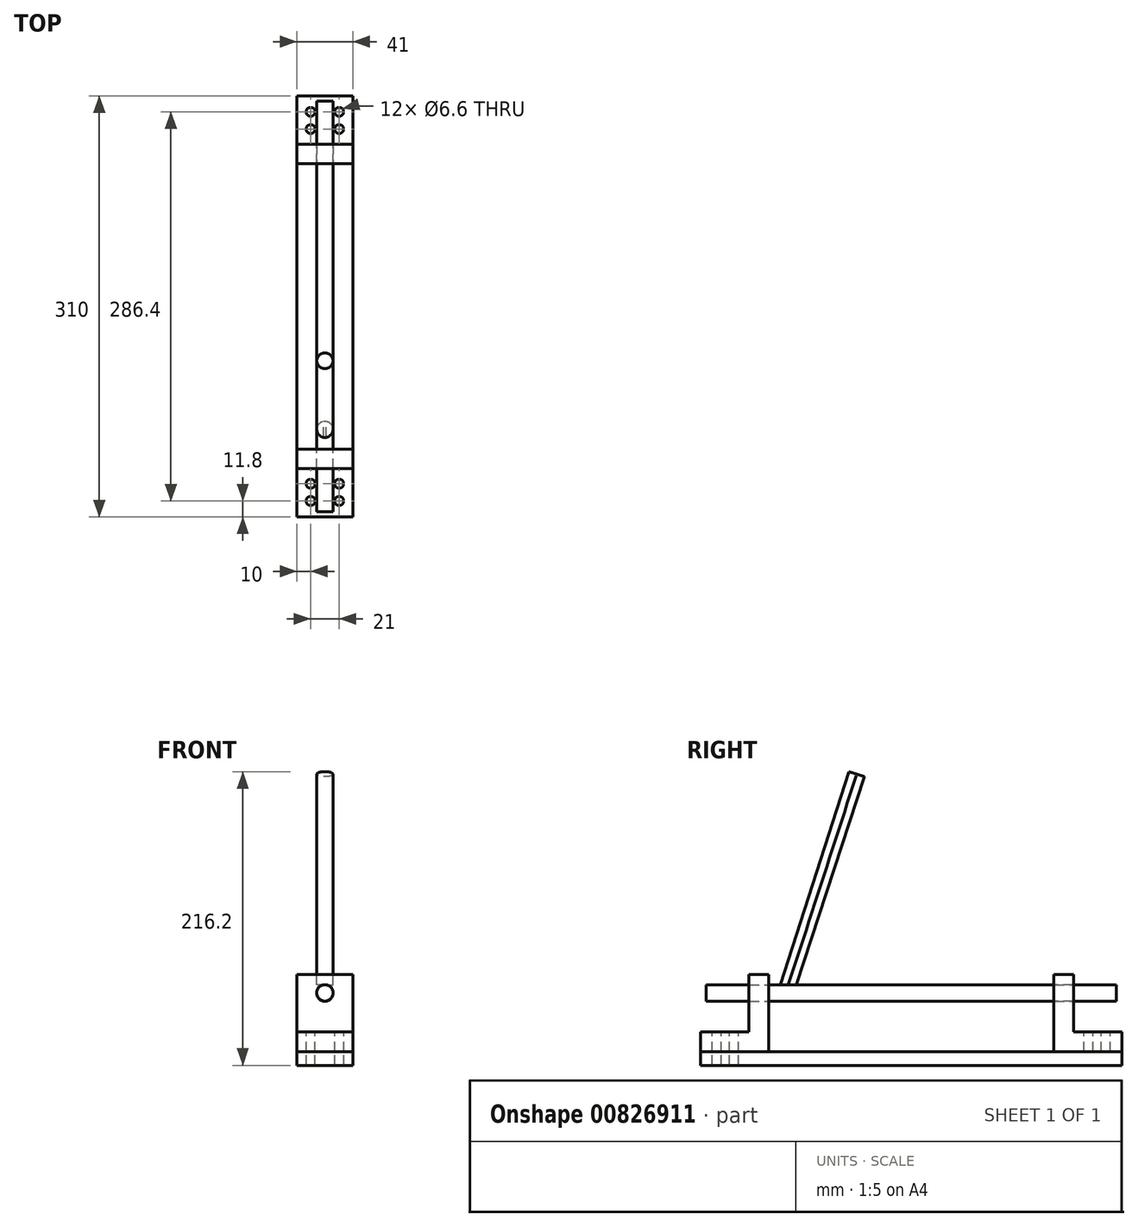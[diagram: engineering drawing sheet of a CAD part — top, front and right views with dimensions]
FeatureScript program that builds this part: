
annotation { "Feature Type Name" : "Feature", "Feature Type Description" : "" }
export const myFeature = defineFeature(function(context is Context, id is Id, definition is map)
    precondition{}
    {
        {
            var Q0;
            Q0=qCreatedBy(makeId("Right.planeOp"),FACE);
            var sketch = newSketch(context, id + "F0", { "sketchPlane" : qUnion([Q0])});
            skLineSegment(sketch, "E0.bottom", {"start": v(-155, -5) * mm, "end": v(155, -5) * mm});
            skLineSegment(sketch, "E0.top", {"start": v(-155, 5) * mm, "end": v(155, 5) * mm});
            skLineSegment(sketch, "E0.left", {"start": v(-155, -5) * mm, "end": v(-155, 5) * mm});
            skLineSegment(sketch, "E0.right", {"start": v(155, -5) * mm, "end": v(155, 5) * mm});
            skSolve(sketch);
        }
        {
            var Q0;
            Q0 = qSketchRegion(id + "F0", true);
            extrude(context, id + "F1", {"entities" : qUnion([Q0]), "depth" : 20.5 * mm, "offsetDistance" : 25.4 * mm, "hasSecondDirection" : true, "secondDirectionOppositeDirection" : true, "secondDirectionDepth" : 20.5 * mm});
        }
        {
            var Q0;
            Q0=qCreatedBy(makeId("Right.planeOp"),FACE);
            var sketch = newSketch(context, id + "F2", { "sketchPlane" : qUnion([Q0])});
            skLineSegment(sketch, "E1.bottom", {"start": v(-155, 5) * mm, "end": v(-105, 5) * mm});
            skLineSegment(sketch, "E1.top", {"start": v(-119.5, 62) * mm, "end": v(-105, 62) * mm});
            skLineSegment(sketch, "E1.left", {"start": v(-155, 5) * mm, "end": v(-155, 19.5) * mm});
            skLineSegment(sketch, "E1.right", {"start": v(-105, 5) * mm, "end": v(-105, 62) * mm});
            skLineSegment(sketch, "E2", {"start": v(-119.5, 62) * mm, "end": v(-119.5, 19.5) * mm});
            skLineSegment(sketch, "E3", {"start": v(-119.5, 19.5) * mm, "end": v(-155, 19.5) * mm});
            skSolve(sketch);
        }
        {
            var Q0;
            Q0=makeQuery(id+"F2.imprint","IMPRINT",FACE,{"disambiguationData":[TD([[makeQuery(id+"F2.imprint","IMPRINT",EDGE,{"derivedFrom":sQuery(id+"F2.wireOp",EDGE,"E1.bottom")}),1.0]])]});
            extrude(context, id + "F3", {"entities" : qUnion([Q0]), "depth" : 20.5 * mm, "offsetDistance" : 25 * mm, "hasSecondDirection" : true, "secondDirectionOppositeDirection" : true, "secondDirectionDepth" : 20.5 * mm});
        }
        {
            var Q0;
            Q0=makeQuery(id+"F3.opExtrude","SWEPT_FACE",FACE,{"disambiguationData":[OSD([sQuery(id+"F2.wireOp",EDGE,"E3")])]});
            var sketch = newSketch(context, id + "F4", { "sketchPlane" : qUnion([Q0])});
            skPoint(sketch, "E4", {"position": v(-10.5, -130.5) * mm});
            skPoint(sketch, "E5", {"position": v(10.5, -130.5) * mm});
            skPoint(sketch, "E6", {"position": v(-10.5, -143.2) * mm});
            skPoint(sketch, "E7", {"position": v(10.5, -143.2) * mm});
            skSolve(sketch);
        }
        {
            var Q0;
            Q0=sQuery(id+"F4.wireOp",VERTEX,"E7");
            var Q1;
            Q1=sQuery(id+"F4.wireOp",VERTEX,"E6");
            var Q2;
            Q2=sQuery(id+"F4.wireOp",VERTEX,"E4");
            var Q3;
            Q3=sQuery(id+"F4.wireOp",VERTEX,"E5");
            var Q4;
            Q4=makeQuery(id+"F1.opExtrude","SWEPT_BODY",BODY,{"disambiguationData":[OSD([sQuery(id+"F0.wireOp",EDGE,"E0.bottom"),sQuery(id+"F0.wireOp",EDGE,"E0.top"),sQuery(id+"F0.wireOp",EDGE,"E0.left"),sQuery(id+"F0.wireOp",EDGE,"E0.right")])]});
            var Q5;
            Q5=makeQuery(id+"F3.opExtrude","SWEPT_BODY",BODY,{"disambiguationData":[OSD([sQuery(id+"F2.wireOp",EDGE,"E1.bottom"),sQuery(id+"F2.wireOp",EDGE,"E1.top"),sQuery(id+"F2.wireOp",EDGE,"E1.left"),sQuery(id+"F2.wireOp",EDGE,"E1.right"),sQuery(id+"F2.wireOp",EDGE,"E2"),sQuery(id+"F2.wireOp",EDGE,"E3")])]});
            hole(context, id + "F5", {"style" : HoleStyle.SIMPLE, "endStyle" : HoleEndStyle.THROUGH, "standardTappedOrClearance" : lookupTablePath({ "standard" : "ISO", "fit" : "Normal", "size" : "M6", "type" : "Clearance" }), "standardBlindInLast" : lookupTablePath({ "fit" : "Standard", "standard" : "ISO", "size" : "M6", "type" : "Clearance" }), "holeDiameter" : 6.6 * mm, "majorDiameter" : 5 * mm, "isTappedThrough" : true, "tappedDepth" : 12 * mm, "tapClearance" : 3, "locations" : qUnion([Q0, Q1, Q2, Q3]), "scope" : qUnion([Q4, Q5])});
        }
        {
            var Q0;
            Q0=makeQuery(id+"F3.opExtrude","SWEPT_FACE",FACE,{"disambiguationData":[OSD([sQuery(id+"F2.wireOp",EDGE,"E1.right")])]});
            var sketch = newSketch(context, id + "F6", { "sketchPlane" : qUnion([Q0])});
            skCircle(sketch, "E8", {"center": v(0, 48.3) * mm, "radius": 6.1 * mm});
            skSolve(sketch);
        }
        {
            var Q0;
            Q0=makeQuery(id+"F6.imprint","IMPRINT",FACE,{"disambiguationData":[TD([[makeQuery(id+"F6.imprint","IMPRINT",EDGE,{"derivedFrom":sQuery(id+"F6.wireOp",EDGE,"E8")}),1.0]])]});
            extrude(context, id + "F7", {"entities" : qUnion([Q0]), "operationType" : NewBodyOperationType.REMOVE, "oppositeDirection" : true, "depth" : 25 * mm, "offsetDistance" : 25 * mm});
        }
        {
            var Q0;
            Q0=makeQuery(id+"F3.opExtrude","SWEPT_BODY",BODY,{"disambiguationData":[OSD([sQuery(id+"F2.wireOp",EDGE,"E1.bottom"),sQuery(id+"F2.wireOp",EDGE,"E1.top"),sQuery(id+"F2.wireOp",EDGE,"E1.left"),sQuery(id+"F2.wireOp",EDGE,"E1.right"),sQuery(id+"F2.wireOp",EDGE,"E2"),sQuery(id+"F2.wireOp",EDGE,"E3")])]});
            var Q1;
            Q1=qCreatedBy(makeId("Front.planeOp"),FACE);
            mirror(context, id + "F8", {"entities" : qUnion([Q0]), "mirrorPlane" : qUnion([Q1])});
        }
        {
            var Q0;
            Q0=qCreatedBy(makeId("Front.planeOp"),FACE);
            var sketch = newSketch(context, id + "F9", { "sketchPlane" : qUnion([Q0])});
            skCircle(sketch, "E9", {"center": v(0, 48.3) * mm, "radius": 6 * mm});
            skSolve(sketch);
        }
        {
            var Q0;
            Q0=makeQuery(id+"F9.imprint","IMPRINT",FACE,{"disambiguationData":[TD([[makeQuery(id+"F9.imprint","IMPRINT",EDGE,{"derivedFrom":sQuery(id+"F9.wireOp",EDGE,"E9")}),1.0]])]});
            extrude(context, id + "F10", {"entities" : qUnion([Q0]), "depth" : 151 * mm, "offsetDistance" : 25 * mm, "hasSecondDirection" : true, "secondDirectionOppositeDirection" : true, "secondDirectionDepth" : 151 * mm});
        }
        {
            var Q0;
            Q0=qCreatedBy(makeId("Right.planeOp"),FACE);
            var sketch = newSketch(context, id + "F11", { "sketchPlane" : qUnion([Q0])});
            skLineSegment(sketch, "E10", {"start": v(-96.5, 54.2) * mm, "end": v(-45.75, 211.2) * mm});
            skLineSegment(sketch, "E11", {"start": v(-45.75, 211.2) * mm, "end": v(-34.33, 207.5) * mm});
            skLineSegment(sketch, "E12", {"start": v(-34.33, 207.5) * mm, "end": v(-84.5, 54.2) * mm});
            skLineSegment(sketch, "E13", {"start": v(-84.5, 54.2) * mm, "end": v(-96.5, 54.2) * mm});
            skSolve(sketch);
        }
        {
            var Q0;
            Q0 = qSketchRegion(id + "F11", true);
            extrude(context, id + "F12", {"entities" : qUnion([Q0]), "operationType" : NewBodyOperationType.ADD, "depth" : 6 * mm, "offsetDistance" : 25 * mm, "hasSecondDirection" : true, "secondDirectionOppositeDirection" : true, "secondDirectionDepth" : 6 * mm});
        }
        {
            var Q0;
            Q0=makeQuery(id+"F12.opExtrude","CAP_EDGE",EDGE,{"disambiguationData":[OSD([sQuery(id+"F11.wireOp",EDGE,"E10")])],"isStart":false});
            var Q1;
            Q1=makeQuery(id+"F12.opExtrude","CAP_EDGE",EDGE,{"disambiguationData":[OSD([sQuery(id+"F11.wireOp",EDGE,"E10")])],"isStart":true});
            var Q2;
            Q2=makeQuery(id+"F12.opExtrude","CAP_EDGE",EDGE,{"disambiguationData":[OSD([sQuery(id+"F11.wireOp",EDGE,"E12")])],"isStart":false});
            var Q3;
            Q3=makeQuery(id+"F12.opExtrude","CAP_EDGE",EDGE,{"disambiguationData":[OSD([sQuery(id+"F11.wireOp",EDGE,"E12")])],"isStart":true});
            fillet(context, id + "F13", {"entities" : qUnion([Q0, Q1, Q2, Q3]), "radius" : 6 * mm, "tangentPropagation" : true, "allowEdgeOverflow" : false});
        }
    });
